# Revit family: Lifelight Pro Recessed Emergency_Hosted_R16
name_source: partatom
category: Lighting Fixtures
revit_build: Autodesk Revit 2016 (Build: 20150220_1215(x64)
units: mm (PartAtom-declared; Revit-internal decimal feet)

## family parameters
Cut with Voids When Loaded = No
Host = Face
Light Source = Yes
Part Type = Normal
Room Calculation Point = No
Round Connector Dimension = Use Diameter
Shared = No

## types (15) — shared parameters
AS2293 = C0=D63, C90=D63
Apparent Load = 2 W
Ballast = Electronic
Color Filter = 16777215
Colour = Plastic - Polycarbonate - White
Default Elevation = 1219 mm
Description = Lifelight Pro, High Performance, Recessed Emergency Light
Dimming Lamp Color Temperature Shift = <None>
Lamp = 2 x 3W LED (Lifetime warranty on the lamp head and loom assembly) No dome cover required
Length = 60 mm  [stored 0.19685 ft]
Manufacturer = Clevertronics
Model = ZLIFE-PRO-SMS
Mounting = Recessed
Operating Mode = Non-Maintained
Operating Voltage = 240 V
Photometric Web File = LIFELIGHT PRO.ies
Round Head = Yes
Square Head = No
Tilt Angle = -90.00°

## per-type parameters (varying)
| type | Battery | Charging Method | Inverter Board | Operating Temperature | Power Consumption | Testing System | Zoneworks Node |
| ZLIFE-PRO | P/N: 1510170, 4 C Cell NiCad Battery Pk. 4.8V 1.8 Ah | Dual-rate | P/N: 8002070, PCA Zoneworks Compatible | 0C to 40C (Ambient) | 2 W | Zoneworks Computerised Testing | P/N: 8001450, Zoneworks Powerline Node |
| CLIFE-PRO-ZW | P/N: 1550230, 3.2V 6400mAh, 200mm Lead | Intelligent current limited constant current | P/N: 8002390, PCA Zoneworks Compatible | 1C to 40C (Ambient) | 1 W | Zoneworks Computerised Testing | P/N: 8001450, Zoneworks Powerline Node |
| CLIFE-PRO-CT | P/N: 1550230, 3.2V 6400mAh, 200mm Lead | Intelligent current limited constant current | P/N: 8002390, PCA Zoneworks Compatible | 1C to 40C (Ambient) | 1 W | Clevertest | P/N: 8001750, Clevertest Node |
| CLIFE-PRO-DATA | P/N: 1550230, 3.2V 6400mAh, 200mm Lead | Intelligent current limited constant current | P/N: 8002390, PCA Zoneworks Compatible | 1C to 40C (Ambient) | 1 W | Zoneworks DATA Testing | P/N: 8001455, Zoneworks DATA Node |
| CLIFE-PRO-DALI | P/N: 1550230, 3.2V 6400mAh, 200mm Lead | Intelligent current limited constant current | P/N: 8002390, PCA Zoneworks Compatible | 1C to 40C (Ambient) | 1 W | DALI Compatible Testing | P/N: 8002200, DALI Node |
| CLIFE-PRO | P/N: 1550230, 3.2V 6400mAh, 200mm Lead | Intelligent current limited constant current | P/N: 8002390, PCA Zoneworks Compatible | 1C to 40C (Ambient) | 0 W | Manual Test Switch |  |
| LLIFE-PRO | P/N: 1530230, 3.3V 5000mAh, 200mm Lead | Intelligent current limited constant current | P/N: 8002390, PCA Zoneworks Compatible | 1C to 40C (Ambient) | 0 W | Manual Test Switch |  |
| LLIFE-PRO-CT | P/N: 1530230, 3.3V 5000mAh, 200mm Lead | Intelligent current limited constant current | P/N: 8002390, PCA Zoneworks Compatible | 1C to 40C (Ambient) | 1 W | Clevertest | P/N: 8001750, Clevertest Node |
| LLIFE-PRO-DALI | P/N: 1530230, 3.3V 5000mAh, 200mm Lead | Intelligent current limited constant current | P/N: 8002390, PCA Zoneworks Compatible | 1C to 40C (Ambient) | 1 W | DALI Compatible Testing | P/N: 8002200, DALI Node |
| LLIFE-PRO-DATA | P/N: 1530230, 3.3V 5000mAh, 200mm Lead | Intelligent current limited constant current | P/N: 8002390, PCA Zoneworks Compatible | 1C to 40C (Ambient) | 1 W | Zoneworks DATA Testing | P/N: 8001455, Zoneworks DATA Node |
| LLIFE-PRO-ZW | P/N: 1530230, 3.3V 5000mAh, 200mm Lead | Intelligent current limited constant current | P/N: 8002390, PCA Zoneworks Compatible | 1C to 40C (Ambient) | 1 W | Zoneworks Computerised Testing | P/N: 8001450, Zoneworks Powerline Node |
| DLIFE-PRO | P/N: 1510170, 4 C Cell NiCad Battery Pk. 4.8V 1.8 Ah | Dual-rate | P/N: 8002070, PCA Zoneworks Compatible | 0C to 40C (Ambient) | 2 W | Clevertest | P/N: 8001730, Clevertest Node |
| PLIFE-PRO | P/N: 1510170, 4 C Cell NiCad Battery Pk. 4.8V 1.8 Ah | Dual-rate | P/N: 8002070, PCA Zoneworks Compatible | 0C to 40C (Ambient) | 2 W | Manual Test Switch |  |
| ZLIFE-PRO-DATA | P/N: 1510170, 4 C Cell NiCad Battery Pk. 4.8V 1.8 Ah | Dual-rate | P/N: 8002070, PCA Zoneworks Compatible | 0C to 40C (Ambient) | 2 W | Zoneworks DATA Testing | P/N: 8001455, Zoneworks DATA Node |
| ZLIFE-PRO-DALI | P/N: 1510170, 4 C Cell NiCad Battery Pk. 4.8V 1.8 Ah | Dual-rate | P/N: 8002070, PCA Zoneworks Compatible | 0C to 40C (Ambient) | 2 W | Zoneworks DATA Testing | P/N: 8002200, Zoneworks DALI Node |

note: [stored X ft] marks values corroborated as IEEE doubles in the binary element streams (Revit-internal decimal feet)

## geometry (parser evidence)
native form markers: Blend x12, Sweep x6
no freeform markers — native parametric forms only
